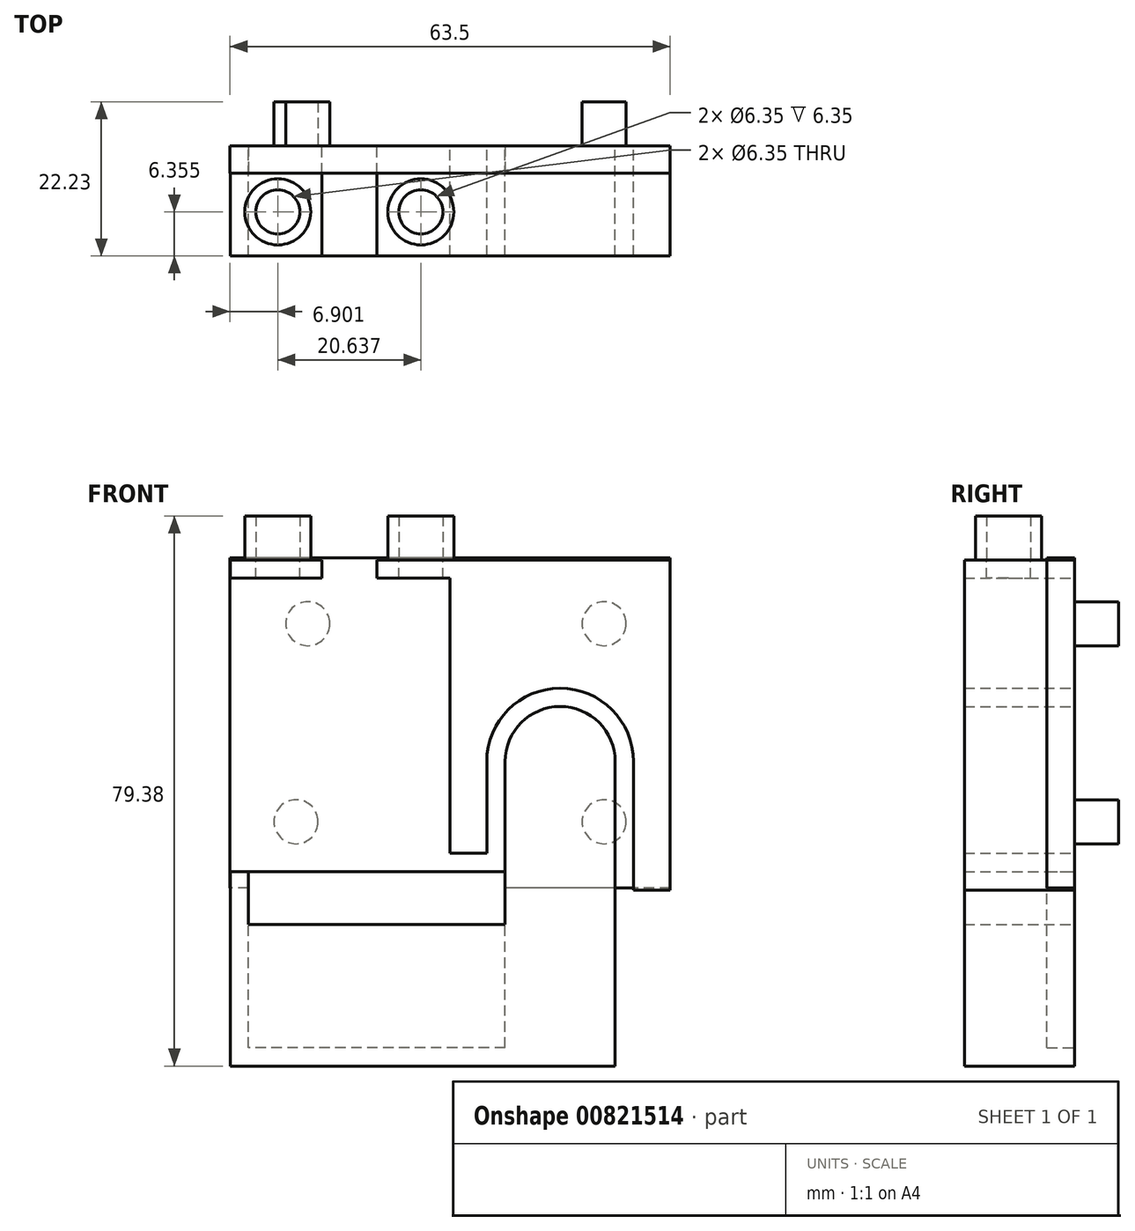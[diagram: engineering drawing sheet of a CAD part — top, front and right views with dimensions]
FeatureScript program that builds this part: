
annotation { "Feature Type Name" : "Feature", "Feature Type Description" : "" }
export const myFeature = defineFeature(function(context is Context, id is Id, definition is map)
    precondition{}
    {
        {
            var Q0;
            Q0=qCreatedBy(makeId("Front.planeOp"),FACE);
            var sketch = newSketch(context, id + "F0", { "sketchPlane" : qUnion([Q0])});
            skLineSegment(sketch, "E0.bottom", {"start": v(-31.75, 44.98) * mm, "end": v(0, 44.98) * mm});
            skLineSegment(sketch, "E0.top", {"start": v(-31.75, 0) * mm, "end": v(0, 0) * mm});
            skLineSegment(sketch, "E0.left", {"start": v(-31.75, 44.98) * mm, "end": v(-31.75, 0) * mm});
            skLineSegment(sketch, "E0.right", {"start": v(0, 44.98) * mm, "end": v(0, 0) * mm});
            skLineSegment(sketch, "E1.bottom", {"start": v(-26.46, 0) * mm, "end": v(-23.81, 0) * mm});
            skLineSegment(sketch, "E1.top", {"start": v(-26.46, 15.88) * mm, "end": v(-23.81, 15.88) * mm});
            skLineSegment(sketch, "E1.left", {"start": v(-26.46, 0) * mm, "end": v(-26.46, 15.87) * mm});
            skLineSegment(sketch, "E1.right", {"start": v(-23.81, 0) * mm, "end": v(-23.81, 15.87) * mm});
            skLineSegment(sketch, "E2.bottom", {"start": v(-7.94, 0) * mm, "end": v(-5.3, 0) * mm});
            skLineSegment(sketch, "E2.top", {"start": v(-7.94, 15.88) * mm, "end": v(-5.3, 15.88) * mm});
            skLineSegment(sketch, "E2.left", {"start": v(-7.94, 0) * mm, "end": v(-7.94, 15.87) * mm});
            skLineSegment(sketch, "E2.right", {"start": v(-5.3, 0) * mm, "end": v(-5.3, 15.87) * mm});
            skArc(sketch, "E3", {"start": v(-5.3, 15.87) * mm, "mid": v(-15.87, 26.46) * mm, "end": v(-26.46, 15.88) * mm});
            skArc(sketch, "E4", {"start": v(-7.94, 15.87) * mm, "mid": v(-15.87, 23.81) * mm, "end": v(-23.81, 15.87) * mm});
            skLineSegment(sketch, "E5.bottom", {"start": v(-26.46, 0) * mm, "end": v(-31.75, 0) * mm});
            skLineSegment(sketch, "E5.top", {"start": v(-26.46, 2.65) * mm, "end": v(-31.75, 2.65) * mm});
            skLineSegment(sketch, "E5.left", {"start": v(-26.46, 0) * mm, "end": v(-26.46, 2.65) * mm});
            skLineSegment(sketch, "E5.right", {"start": v(-31.75, 0) * mm, "end": v(-31.75, 2.65) * mm});
            skLineSegment(sketch, "E6.bottom", {"start": v(-31.75, 44.98) * mm, "end": v(-63.47, 44.98) * mm});
            skLineSegment(sketch, "E6.top", {"start": v(-31.75, 42.34) * mm, "end": v(-63.47, 42.34) * mm});
            skLineSegment(sketch, "E6.left", {"start": v(-31.75, 44.98) * mm, "end": v(-31.75, 42.34) * mm});
            skLineSegment(sketch, "E6.right", {"start": v(-63.47, 44.98) * mm, "end": v(-63.47, 42.34) * mm});
            skLineSegment(sketch, "E7.bottom", {"start": v(-63.47, 42.34) * mm, "end": v(-60.82, 42.34) * mm});
            skLineSegment(sketch, "E7.top", {"start": v(-63.47, 0) * mm, "end": v(-60.82, 0) * mm});
            skLineSegment(sketch, "E7.left", {"start": v(-63.47, 42.34) * mm, "end": v(-63.47, 0) * mm});
            skLineSegment(sketch, "E7.right", {"start": v(-60.82, 42.34) * mm, "end": v(-60.82, 0) * mm});
            skLineSegment(sketch, "E8.bottom", {"start": v(-63.47, 0) * mm, "end": v(0, 0) * mm});
            skLineSegment(sketch, "E8.top", {"start": v(-63.47, -2.65) * mm, "end": v(0, -2.65) * mm});
            skLineSegment(sketch, "E8.left", {"start": v(-63.47, 0) * mm, "end": v(-63.47, -2.65) * mm});
            skLineSegment(sketch, "E8.right", {"start": v(0, 0) * mm, "end": v(0, -2.65) * mm});
            skLineSegment(sketch, "E9.top", {"start": v(-7.94, -2.65) * mm, "end": v(-5.3, -2.65) * mm});
            skLineSegment(sketch, "E9.left", {"start": v(-7.94, 0) * mm, "end": v(-7.94, -2.65) * mm});
            skLineSegment(sketch, "E9.right", {"start": v(-5.3, 0) * mm, "end": v(-5.3, -2.65) * mm});
            skLineSegment(sketch, "E10.bottom", {"start": v(-58.18, 44.98) * mm, "end": v(-55.53, 44.98) * mm});
            skLineSegment(sketch, "E10.top", {"start": v(-58.18, 42.34) * mm, "end": v(-55.53, 42.34) * mm});
            skLineSegment(sketch, "E11.bottom", {"start": v(-50.25, 44.98) * mm, "end": v(-42.31, 44.98) * mm});
            skLineSegment(sketch, "E11.top", {"start": v(-50.25, 42.34) * mm, "end": v(-42.31, 42.34) * mm});
            skLineSegment(sketch, "E11.left", {"start": v(-50.25, 44.98) * mm, "end": v(-50.25, 42.34) * mm});
            skLineSegment(sketch, "E11.right", {"start": v(-42.31, 44.98) * mm, "end": v(-42.31, 42.34) * mm});
            skLineSegment(sketch, "E12.bottom", {"start": v(-37.04, 44.98) * mm, "end": v(-34.4, 44.98) * mm});
            skLineSegment(sketch, "E12.top", {"start": v(-37.04, 42.34) * mm, "end": v(-34.4, 42.34) * mm});
            skSolve(sketch);
        }
        {
            var Q0;
            Q0=makeQuery(id+"F0.imprint","IMPRINT",FACE,{"disambiguationData":[TD([[makeQuery(id+"F0.imprint","IMPRINT",EDGE,{"derivedFrom":sQuery(id+"F0.wireOp",EDGE,"E0.bottom")}),-1.0]])]});
            var Q1;
            {var subQ0=sQuery(id+"F0.wireOp",EDGE,"E1.right");Q1=makeQuery(id+"F0.imprint","IMPRINT",FACE,{"disambiguationData":[TD([[makeQuery(id+"F0.imprint","IMPRINT",EDGE,{"derivedFrom":subQ0}),-1.0]])]});}
            var Q2;
            {var subQ6=sQuery(id+"F0.wireOp",EDGE,"E8.left");Q2=makeQuery(id+"F0.imprint","IMPRINT",FACE,{"disambiguationData":[TD([[makeQuery(id+"F0.imprint","IMPRINT",EDGE,{"derivedFrom":subQ6}),1.0]])]});}
            var Q3;
            {var subQ0=sQuery(id+"F0.wireOp",EDGE,"E8.right");Q3=makeQuery(id+"F0.imprint","IMPRINT",FACE,{"disambiguationData":[TD([[makeQuery(id+"F0.imprint","IMPRINT",EDGE,{"derivedFrom":subQ0}),-1.0]])]});}
            var Q4;
            Q4=makeQuery(id+"F0.imprint","IMPRINT",FACE,{"disambiguationData":[TD([[makeQuery(id+"F0.imprint","IMPRINT",EDGE,{"derivedFrom":sQuery(id+"F0.wireOp",EDGE,"E7.bottom")}),-1.0]])]});
            var Q5;
            {var subQ1=sQuery(id+"F0.wireOp",EDGE,"E6.right");Q5=makeQuery(id+"F0.imprint","IMPRINT",FACE,{"disambiguationData":[TD([[makeQuery(id+"F0.imprint","IMPRINT",EDGE,{"derivedFrom":subQ1}),1.0]])]});}
            var Q6;
            {var subQ0=sQuery(id+"F0.wireOp",EDGE,"E10.right");Q6=makeQuery(id+"F0.imprint","IMPRINT",FACE,{"disambiguationData":[TD([[makeQuery(id+"F0.imprint","IMPRINT",EDGE,{"derivedFrom":subQ0}),1.0]])]});}
            var Q7;
            {var subQ0=sQuery(id+"F0.wireOp",EDGE,"E11.right");Q7=makeQuery(id+"F0.imprint","IMPRINT",FACE,{"disambiguationData":[TD([[makeQuery(id+"F0.imprint","IMPRINT",EDGE,{"derivedFrom":subQ0}),1.0]])]});}
            var Q8;
            {var subQ0=sQuery(id+"F0.wireOp",EDGE,"E6.left");Q8=makeQuery(id+"F0.imprint","IMPRINT",FACE,{"disambiguationData":[TD([[makeQuery(id+"F0.imprint","IMPRINT",EDGE,{"derivedFrom":subQ0}),-1.0]])]});}
            extrude(context, id + "F1", {"entities" : qUnion([Q0, Q1, Q2, Q3, Q4, Q5, Q6, Q7, Q8]), "depth" : 15.88 * mm, "offsetDistance" : 25.4 * mm});
        }
        {
            var Q0;
            Q0=qCreatedBy(makeId("Front.planeOp"),FACE);
            var sketch = newSketch(context, id + "F2", { "sketchPlane" : qUnion([Q0])});
            skLineSegment(sketch, "E13.bottom", {"start": v(0, 45.3) * mm, "end": v(-63.5, 45.3) * mm});
            skLineSegment(sketch, "E13.top", {"start": v(0, -2.33) * mm, "end": v(-63.5, -2.33) * mm});
            skLineSegment(sketch, "E13.left", {"start": v(0, 45.3) * mm, "end": v(0, -2.33) * mm});
            skLineSegment(sketch, "E13.right", {"start": v(-63.5, 45.3) * mm, "end": v(-63.5, -2.33) * mm});
            skCircle(sketch, "E14", {"center": v(-9.53, 35.77) * mm, "radius": 3.18 * mm});
            skCircle(sketch, "E15", {"center": v(-52.28, 35.77) * mm, "radius": 3.18 * mm});
            skCircle(sketch, "E16", {"center": v(-53.97, 7.2) * mm, "radius": 3.18 * mm});
            skCircle(sketch, "E17", {"center": v(-9.52, 7.2) * mm, "radius": 3.18 * mm});
            skSolve(sketch);
        }
        {
            var Q0;
            Q0=qSketchRegion(id+"F2",true);
            var Q1;
            Q1=makeQuery(id+"F2.imprint","IMPRINT",FACE,{"disambiguationData":[TD([[makeQuery(id+"F2.imprint","IMPRINT",EDGE,{"derivedFrom":sQuery(id+"F2.wireOp",EDGE,"E15")}),1.0]])]});
            var Q2;
            Q2=makeQuery(id+"F2.imprint","IMPRINT",FACE,{"disambiguationData":[TD([[makeQuery(id+"F2.imprint","IMPRINT",EDGE,{"derivedFrom":sQuery(id+"F2.wireOp",EDGE,"E16")}),1.0]])]});
            var Q3;
            Q3=makeQuery(id+"F2.imprint","IMPRINT",FACE,{"disambiguationData":[TD([[makeQuery(id+"F2.imprint","IMPRINT",EDGE,{"derivedFrom":sQuery(id+"F2.wireOp",EDGE,"E17")}),1.0]])]});
            var Q4;
            Q4=makeQuery(id+"F2.imprint","IMPRINT",FACE,{"disambiguationData":[TD([[makeQuery(id+"F2.imprint","IMPRINT",EDGE,{"derivedFrom":sQuery(id+"F2.wireOp",EDGE,"E14")}),1.0]])]});
            extrude(context, id + "F3", {"entities" : qUnion([Q0, Q1, Q2, Q3, Q4]), "depth" : 3.97 * mm, "offsetDistance" : 25.4 * mm});
        }
        {
            var Q0;
            Q0=makeQuery(id+"F2.imprint","IMPRINT",FACE,{"disambiguationData":[TD([[makeQuery(id+"F2.imprint","IMPRINT",EDGE,{"derivedFrom":sQuery(id+"F2.wireOp",EDGE,"E14")}),1.0]])]});
            var Q1;
            Q1=makeQuery(id+"F2.imprint","IMPRINT",FACE,{"disambiguationData":[TD([[makeQuery(id+"F2.imprint","IMPRINT",EDGE,{"derivedFrom":sQuery(id+"F2.wireOp",EDGE,"E15")}),1.0]])]});
            var Q2;
            Q2=makeQuery(id+"F2.imprint","IMPRINT",FACE,{"disambiguationData":[TD([[makeQuery(id+"F2.imprint","IMPRINT",EDGE,{"derivedFrom":sQuery(id+"F2.wireOp",EDGE,"E17")}),1.0]])]});
            var Q3;
            Q3=makeQuery(id+"F2.imprint","IMPRINT",FACE,{"disambiguationData":[TD([[makeQuery(id+"F2.imprint","IMPRINT",EDGE,{"derivedFrom":sQuery(id+"F2.wireOp",EDGE,"E16")}),1.0]])]});
            var Q4;
            Q4=sQuery(id+"F2.wireOp",EDGE,"E14");
            var Q5;
            Q5=sQuery(id+"F2.wireOp",EDGE,"E15");
            var Q6;
            Q6=sQuery(id+"F2.wireOp",EDGE,"E17");
            var Q7;
            Q7=sQuery(id+"F2.wireOp",EDGE,"E16");
            extrude(context, id + "F4", {"entities" : qUnion([Q0, Q1, Q2, Q3]), "surfaceEntities" : qUnion([Q4, Q5, Q6, Q7]), "oppositeDirection" : true, "depth" : 6.35 * mm, "offsetDistance" : 25.4 * mm});
        }
        {
            var Q0;
            Q0=makeQuery(id+"F1.opExtrude","SWEPT_FACE",FACE,{"disambiguationData":[OSD([sQuery(id+"F0.wireOp",EDGE,"E6.bottom"),sQuery(id+"F0.wireOp",EDGE,"E10.bottom")])]});
            var sketch = newSketch(context, id + "F5", { "sketchPlane" : qUnion([Q0])});
            skCircle(sketch, "E18", {"center": v(-56.6, -9.52) * mm, "radius": 3.18 * mm});
            skCircle(sketch, "E19", {"center": v(-35.96, -9.52) * mm, "radius": 3.18 * mm});
            skCircle(sketch, "E20", {"center": v(-56.6, -9.52) * mm, "radius": 4.76 * mm});
            skCircle(sketch, "E21", {"center": v(-35.96, -9.52) * mm, "radius": 4.76 * mm});
            skSolve(sketch);
        }
        {
            var Q0;
            Q0=qSketchRegion(id+"F5",true);
            extrude(context, id + "F6", {"entities" : qUnion([Q0]), "depth" : 6.35 * mm, "offsetDistance" : 25.4 * mm});
        }
        {
            var Q0;
            Q0=makeQuery(id+"F1.opExtrude","SWEPT_FACE",FACE,{"disambiguationData":[OSD([sQuery(id+"F0.wireOp",EDGE,"E6.bottom"),sQuery(id+"F0.wireOp",EDGE,"E10.bottom")])]});
            var sketch = newSketch(context, id + "F7", { "sketchPlane" : qUnion([Q0])});
            skCircle(sketch, "E22", {"center": v(-35.96, -9.52) * mm, "radius": 3.18 * mm});
            skCircle(sketch, "E23", {"center": v(-56.6, -9.52) * mm, "radius": 3.18 * mm});
            skSolve(sketch);
        }
        {
            var Q0;
            Q0=qSketchRegion(id+"F7",true);
            extrude(context, id + "F8", {"entities" : qUnion([Q0]), "operationType" : NewBodyOperationType.REMOVE, "oppositeDirection" : true, "depth" : 25.4 * mm, "offsetDistance" : 25.4 * mm});
        }
        {
            var Q0;
            {var subQ0=sQuery(id+"F0.wireOp",EDGE,"E8.top");Q0=makeQuery(id+"F1.opExtrude","SWEPT_FACE",FACE,{"disambiguationData":[OSD([subQ0]),TDD([makeQuery(id+"F0.imprint","IMPRINT",EDGE,{"disambiguationData":[TD([[makeQuery(id+"F0.imprint","INTERSECT",VERTEX,{"derivedFrom":[subQ0,sQuery(id+"F0.wireOp",EDGE,"E8.left")]}),-1.0]])],"derivedFrom":subQ0})])]});}
            var sketch = newSketch(context, id + "F9", { "sketchPlane" : qUnion([Q0])});
            skLineSegment(sketch, "E24.bottom", {"start": v(-63.47, 0) * mm, "end": v(-7.94, 0) * mm});
            skLineSegment(sketch, "E24.top", {"start": v(-63.47, 15.88) * mm, "end": v(-7.94, 15.88) * mm});
            skLineSegment(sketch, "E24.left", {"start": v(-63.47, 0) * mm, "end": v(-63.47, 15.88) * mm});
            skLineSegment(sketch, "E24.right", {"start": v(-7.94, 0) * mm, "end": v(-7.94, 15.88) * mm});
            skSolve(sketch);
        }
        {
            var Q0;
            Q0 = qSketchRegion(id + "F9", true);
            extrude(context, id + "F10", {"entities" : qUnion([Q0]), "operationType" : NewBodyOperationType.ADD, "depth" : 25.4 * mm, "offsetDistance" : 25.4 * mm});
        }
        {
            var Q0;
            {var subQ0=sQuery(id+"F0.wireOp",EDGE,"E8.bottom");var subQ1=makeQuery(id+"F0.imprint","INTERSECT",VERTEX,{"derivedFrom":[sQuery(id+"F0.wireOp",EDGE,"E5.left"),subQ0]});var subQ2=makeQuery(id+"F0.imprint","INTERSECT",VERTEX,{"derivedFrom":[sQuery(id+"F0.wireOp",EDGE,"E5.right"),subQ0]});Q0=makeQuery(id+"F1.opExtrude","SWEPT_FACE",FACE,{"disambiguationData":[OSD([subQ0]),TDD([makeQuery(id+"F0.imprint","IMPRINT",EDGE,{"disambiguationData":[TD([[subQ2,1.0]])],"derivedFrom":subQ0}),makeQuery(id+"F0.imprint","IMPRINT",EDGE,{"disambiguationData":[TD([[subQ1,1.0]])],"derivedFrom":subQ0}),makeQuery(id+"F0.imprint","IMPRINT",EDGE,{"disambiguationData":[TD([[makeQuery(id+"F0.imprint","INTERSECT",VERTEX,{"derivedFrom":[sQuery(id+"F0.wireOp",EDGE,"E1.right"),subQ0]}),1.0]])],"derivedFrom":subQ0})])]});}
            var sketch = newSketch(context, id + "F11", { "sketchPlane" : qUnion([Q0])});
            skLineSegment(sketch, "E25.bottom", {"start": v(-60.82, -15.88) * mm, "end": v(-23.81, -15.88) * mm});
            skLineSegment(sketch, "E25.top", {"start": v(-60.82, 0) * mm, "end": v(-23.81, 0) * mm});
            skLineSegment(sketch, "E25.left", {"start": v(-60.82, -15.88) * mm, "end": v(-60.82, 0) * mm});
            skLineSegment(sketch, "E25.right", {"start": v(-23.81, -15.88) * mm, "end": v(-23.81, 0) * mm});
            skSolve(sketch);
        }
        {
            var Q0;
            Q0 = qSketchRegion(id + "F11", true);
            extrude(context, id + "F12", {"entities" : qUnion([Q0]), "operationType" : NewBodyOperationType.REMOVE, "oppositeDirection" : true, "depth" : 7.62 * mm, "offsetDistance" : 25.4 * mm});
        }
        {
            var Q0;
            Q0=makeQuery(id+"F12.boolean.opBoolean","COPY",FACE,{"derivedFrom":makeQuery(id+"F12.opExtrude","CAP_FACE",FACE,{"disambiguationData":[OSD([sQuery(id+"F11.wireOp",EDGE,"E25.bottom"),sQuery(id+"F11.wireOp",EDGE,"E25.top"),sQuery(id+"F11.wireOp",EDGE,"E25.left"),sQuery(id+"F11.wireOp",EDGE,"E25.right")])],"isStart":true})});
            var sketch = newSketch(context, id + "F13", { "sketchPlane" : qUnion([Q0])});
            skLineSegment(sketch, "E26.bottom", {"start": v(-60.82, 3.97) * mm, "end": v(-23.81, 3.97) * mm});
            skLineSegment(sketch, "E26.top", {"start": v(-60.82, 0) * mm, "end": v(-23.81, 0) * mm});
            skLineSegment(sketch, "E26.left", {"start": v(-60.82, 3.97) * mm, "end": v(-60.82, 0) * mm});
            skLineSegment(sketch, "E26.right", {"start": v(-23.81, 3.97) * mm, "end": v(-23.81, 0) * mm});
            skSolve(sketch);
        }
        {
            var Q0;
            Q0 = qSketchRegion(id + "F13", true);
            extrude(context, id + "F14", {"entities" : qUnion([Q0]), "depth" : 25.4 * mm, "offsetDistance" : 25.4 * mm});
        }
    });
